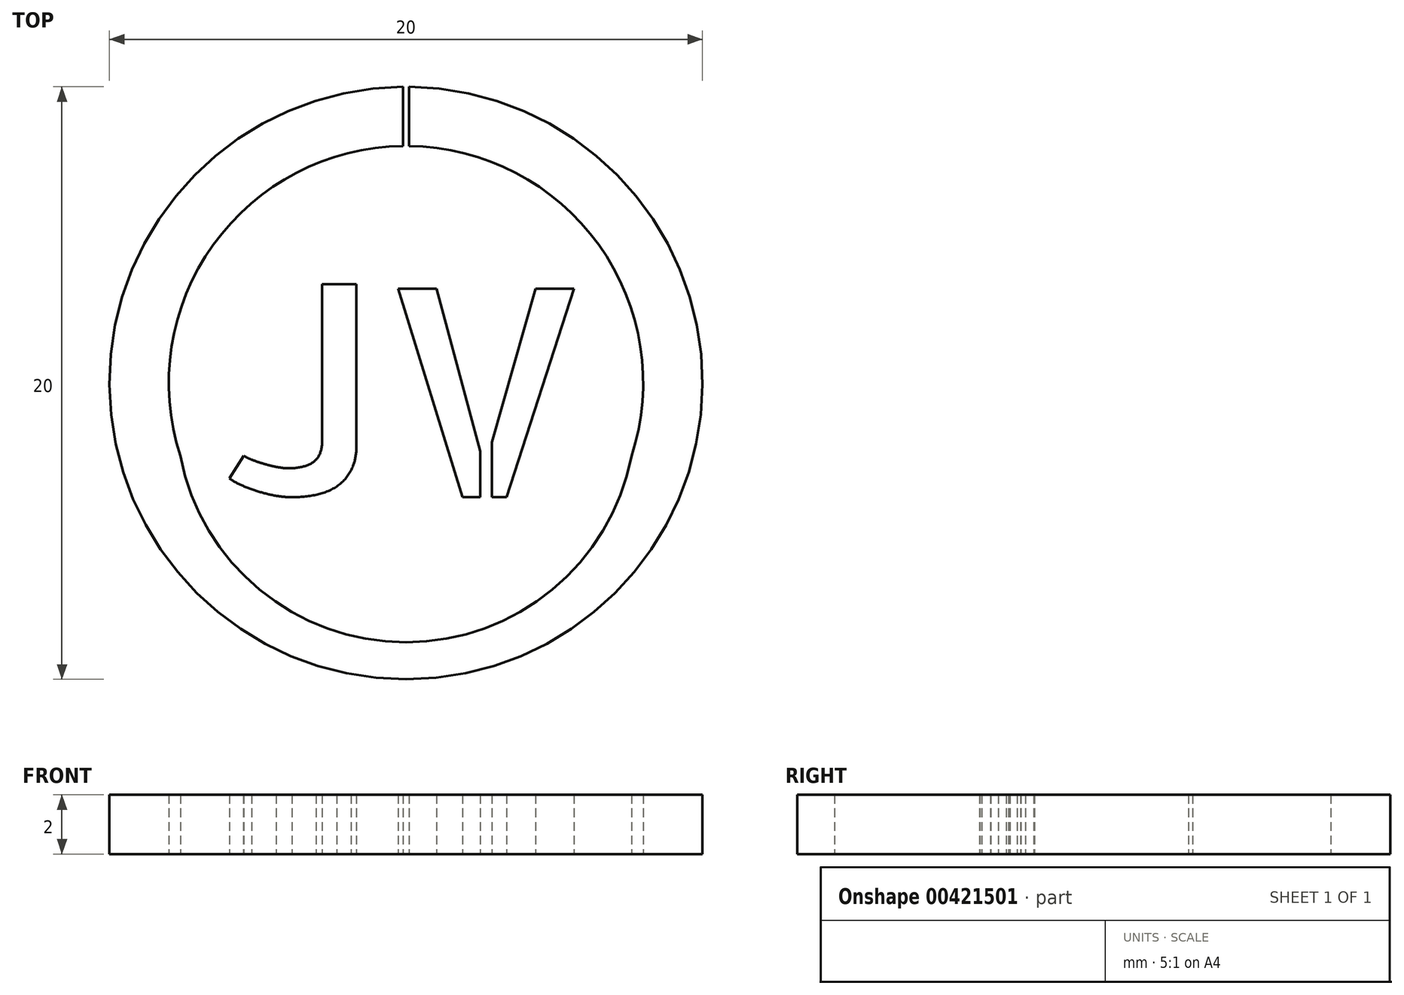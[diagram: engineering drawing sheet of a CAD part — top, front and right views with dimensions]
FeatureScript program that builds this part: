
annotation { "Feature Type Name" : "Feature", "Feature Type Description" : "" }
export const myFeature = defineFeature(function(context is Context, id is Id, definition is map)
    precondition{}
    {
        {
            var Q0;
            Q0=qCreatedBy(makeId("Top.planeOp"),FACE);
            var sketch = newSketch(context, id + "F0", { "sketchPlane" : qUnion([Q0])});
            skCircle(sketch, "E0", {"center": v(0, 0) * mm, "radius": 10 * mm});
            skCircle(sketch, "E1", {"center": v(0, 0) * mm, "radius": 8 * mm});
            skCircle(sketch, "E2", {"center": v(0, -1) * mm, "radius": 7.75 * mm});
            skText(sketch, "E3", { "text": "JV", "fontName": "AllertaStencil-Regular.ttf"});
            skLineSegment(sketch, "E4", {"start": v(0.1, 10) * mm, "end": v(0.1, 8) * mm});
            skLineSegment(sketch, "E5", {"start": v(-0.1, 10) * mm, "end": v(-0.1, 8) * mm});
            skCircle(sketch, "E6", {"center": v(0, 6.75) * mm, "radius": 1.5 * mm});
            const initialGuessF0  = {"E3": [-0.0062, -0.00381, 1, 0, 0.007]};
            skSetInitialGuess(sketch, initialGuessF0);
            skSolve(sketch);
        }
        {
            var Q0;
            {var subQ0=sQuery(id+"F0.wireOp",EDGE,"E4");Q0=makeQuery(id+"F0.imprint","IMPRINT",FACE,{"disambiguationData":[TD([[makeQuery(id+"F0.imprint","IMPRINT",EDGE,{"derivedFrom":subQ0}),1.0]])]});}
            var Q1;
            {var subQ0=sQuery(id+"F0.wireOp",EDGE,"E2");var subQ1=sQuery(id+"F0.wireOp",EDGE,"E1");var subQ2=makeQuery(id+"F0.imprint","INTERSECT",VERTEX,{"disambiguationData":[OD(0.0)],"derivedFrom":[subQ1,subQ0]});Q1=makeQuery(id+"F0.imprint","IMPRINT",FACE,{"disambiguationData":[TD([[makeQuery(id+"F0.imprint","IMPRINT",EDGE,{"disambiguationData":[TD([[subQ2,-1.0]])],"derivedFrom":subQ1}),-1.0]])]});}
            var Q2;
            {var subQ0=sQuery(id+"F0.wireOp",EDGE,"E5");var subQ1=sQuery(id+"F0.wireOp",EDGE,"E1");var subQ2=makeQuery(id+"F0.imprint","INTERSECT",VERTEX,{"derivedFrom":[subQ1,subQ0]});Q2=makeQuery(id+"F0.imprint","IMPRINT",FACE,{"disambiguationData":[TD([[makeQuery(id+"F0.imprint","IMPRINT",EDGE,{"disambiguationData":[TD([[subQ2,-1.0]])],"derivedFrom":subQ1}),-1.0]])]});}
            var Q3;
            {var subQ5=sQuery(id+"F0.wireOp",EDGE,"E4");var subQ6=sQuery(id+"F0.wireOp",EDGE,"E0");var subQ7=makeQuery(id+"F0.imprint","INTERSECT",VERTEX,{"derivedFrom":[subQ6,subQ5]});Q3=makeQuery(id+"F0.imprint","IMPRINT",FACE,{"disambiguationData":[TD([[makeQuery(id+"F0.imprint","IMPRINT",EDGE,{"disambiguationData":[TD([[subQ7,1.0]])],"derivedFrom":subQ6}),1.0]])]});}
            extrude(context, id + "F1", {"entities" : qUnion([Q0, Q1, Q2, Q3]), "depth" : 2 * mm, "offsetDistance" : 25 * mm});
        }
        {
            var Q0;
            Q0=makeQuery(id+"F0.imprint","IMPRINT",FACE,{"disambiguationData":[TD([[makeQuery(id+"F0.imprint","IMPRINT",EDGE,{"derivedFrom":sQuery(id+"F0.wireOp",EDGE,"E2")}),1.0]])]});
            var Q1;
            {var subQ0=sQuery(id+"F0.wireOp",EDGE,"E4");Q1=makeQuery(id+"F0.imprint","IMPRINT",FACE,{"disambiguationData":[TD([[makeQuery(id+"F0.imprint","IMPRINT",EDGE,{"derivedFrom":subQ0}),1.0]])]});}
            var Q2;
            Q2=makeQuery(id+"F0.imprint","IMPRINT",FACE,{"disambiguationData":[TD([[makeQuery(id+"F0.imprint","IMPRINT",EDGE,{"derivedFrom":sQuery(id+"F0.wireOp",EDGE,"E3.sketch_text.stroke-0")}),1.0]])]});
            extrude(context, id + "F2", {"entities" : qUnion([Q0, Q1, Q2]), "operationType" : NewBodyOperationType.ADD, "depth" : 1 * mm, "offsetDistance" : 25 * mm});
        }
        {
            var Q0;
            Q0=makeQuery(id+"F0.imprint","IMPRINT",FACE,{"disambiguationData":[TD([[makeQuery(id+"F0.imprint","IMPRINT",EDGE,{"derivedFrom":sQuery(id+"F0.wireOp",EDGE,"E3.sketch_text.stroke-0")}),-1.0]])]});
            var Q1;
            Q1=makeQuery(id+"F0.imprint","IMPRINT",FACE,{"disambiguationData":[TD([[makeQuery(id+"F0.imprint","IMPRINT",EDGE,{"derivedFrom":sQuery(id+"F0.wireOp",EDGE,"E3.sketch_text.stroke-18")}),-1.0]])]});
            var Q2;
            Q2=makeQuery(id+"F0.imprint","IMPRINT",FACE,{"disambiguationData":[TD([[makeQuery(id+"F0.imprint","IMPRINT",EDGE,{"derivedFrom":sQuery(id+"F0.wireOp",EDGE,"E3.sketch_text.stroke-23")}),-1.0]])]});
            extrude(context, id + "F3", {"entities" : qUnion([Q0, Q1, Q2]), "operationType" : NewBodyOperationType.ADD, "depth" : 2 * mm, "offsetDistance" : 25 * mm});
        }
        {
            var Q0;
            {var subQ0=sQuery(id+"F0.wireOp",EDGE,"E6");var subQ1=sQuery(id+"F0.wireOp",EDGE,"E2");var subQ2=makeQuery(id+"F0.imprint","INTERSECT",VERTEX,{"disambiguationData":[OD(0.0)],"derivedFrom":[subQ1,subQ0]});Q0=makeQuery(id+"F0.imprint","IMPRINT",FACE,{"disambiguationData":[TD([[makeQuery(id+"F0.imprint","IMPRINT",EDGE,{"disambiguationData":[TD([[subQ2,1.0]])],"derivedFrom":subQ1}),1.0]])]});}
            extrude(context, id + "F4", {"entities" : qUnion([Q0]), "operationType" : NewBodyOperationType.REMOVE, "depth" : 25 * mm, "offsetDistance" : 25 * mm});
        }
    });
